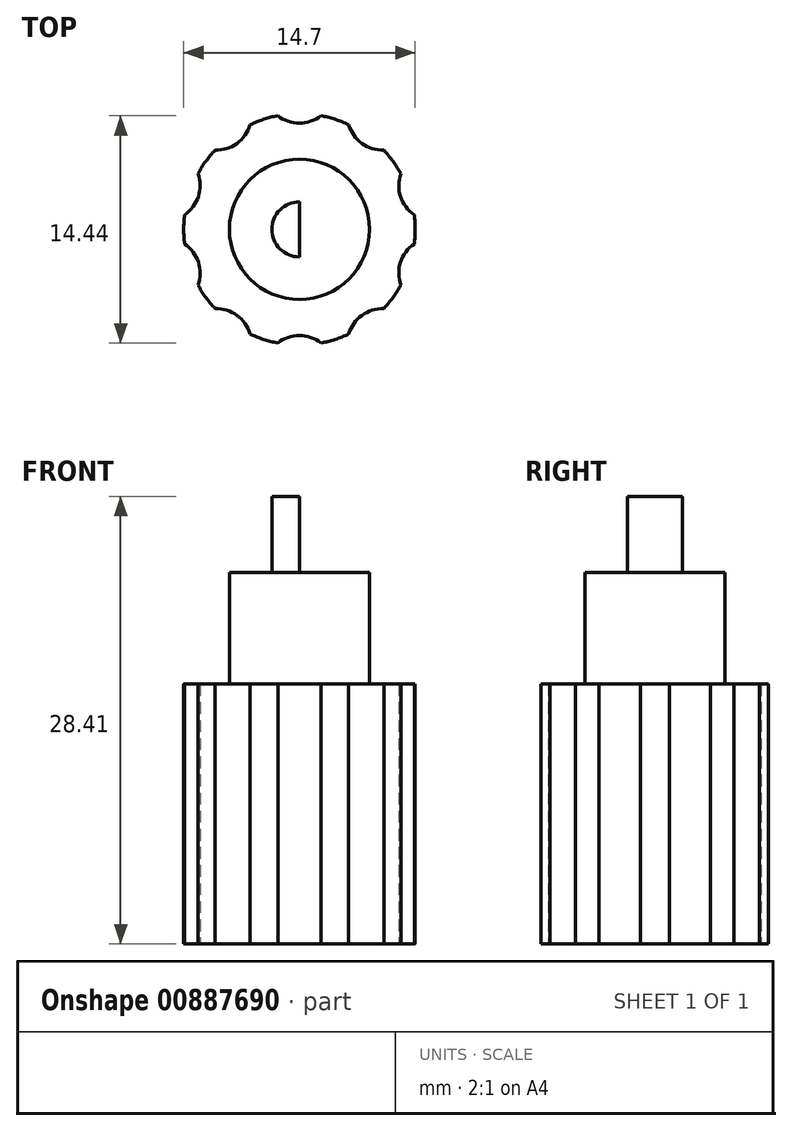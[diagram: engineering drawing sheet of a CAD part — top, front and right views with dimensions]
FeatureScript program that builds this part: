
annotation { "Feature Type Name" : "Feature", "Feature Type Description" : "" }
export const myFeature = defineFeature(function(context is Context, id is Id, definition is map)
    precondition{}
    {
        {
            var Q0;
            Q0=qCreatedBy(makeId("Top.planeOp"),FACE);
            var sketch = newSketch(context, id + "F0", { "sketchPlane" : qUnion([Q0])});
            skCircle(sketch, "E0", {"center": v(0, 0) * mm, "radius": 7.35 * mm});
            skSolve(sketch);
        }
        {
            var Q0;
            Q0 = qSketchRegion(id + "F0", true);
            extrude(context, id + "F1", {"entities" : qUnion([Q0]), "depth" : 16.5 * mm, "offsetDistance" : 25 * mm});
        }
        {
            var Q0;
            Q0=makeQuery(id+"F1.opExtrude","CAP_FACE",FACE,{"disambiguationData":[OSD([sQuery(id+"F0.wireOp",EDGE,"E0")])],"isStart":false});
            var sketch = newSketch(context, id + "F2", { "sketchPlane" : qUnion([Q0])});
            skCircle(sketch, "E1", {"center": v(0, 0) * mm, "radius": 4.45 * mm});
            skSolve(sketch);
        }
        {
            var Q0;
            Q0 = qSketchRegion(id + "F2", true);
            extrude(context, id + "F3", {"entities" : qUnion([Q0]), "operationType" : NewBodyOperationType.ADD, "depth" : 7.08 * mm, "offsetDistance" : 25 * mm});
        }
        {
            var Q0;
            Q0=makeQuery(id+"F3.opExtrude","CAP_FACE",FACE,{"disambiguationData":[OSD([sQuery(id+"F2.wireOp",EDGE,"E1")])],"isStart":false});
            var sketch = newSketch(context, id + "F4", { "sketchPlane" : qUnion([Q0])});
            skSolve(sketch);
        }
        {
            var Q0;
            Q0=makeQuery(id+"F4.imprint","IMPRINT",FACE,{"disambiguationData":[TD([[makeQuery(id+"F4.imprint","IMPRINT",EDGE,{"derivedFrom":makeQuery(id+"F3.opExtrude","CAP_EDGE",EDGE,{"disambiguationData":[OSD([sQuery(id+"F2.wireOp",EDGE,"E1")])],"isStart":false})}),1.0]])]});
            var sketch = newSketch(context, id + "F5", { "sketchPlane" : qUnion([Q0])});
            skArc(sketch, "E2", {"start": v(0, 1.75) * mm, "mid": v(-1.75, 0) * mm, "end": v(0, -1.75) * mm});
            skLineSegment(sketch, "E3", {"start": v(0, -1.75) * mm, "end": v(0, 1.75) * mm});
            skSolve(sketch);
        }
        {
            var Q0;
            Q0 = qSketchRegion(id + "F5", true);
            extrude(context, id + "F6", {"entities" : qUnion([Q0]), "operationType" : NewBodyOperationType.ADD, "depth" : 4.83 * mm, "offsetDistance" : 25 * mm});
        }
        {
            var Q0;
            Q0=makeQuery(id+"F1.opExtrude","CAP_FACE",FACE,{"disambiguationData":[OSD([sQuery(id+"F0.wireOp",EDGE,"E0")])],"isStart":true});
            var sketch = newSketch(context, id + "F7", { "sketchPlane" : qUnion([Q0])});
            skLineSegment(sketch, "E4", {"start": v(0, 0) * mm, "end": v(0, -9) * mm, "construction": true});
            skCircle(sketch, "E5", {"center": v(0, -9) * mm, "radius": 2.25 * mm});
            skCircle(sketch, "E6.1.0", {"center": v(5.3, -7.28) * mm, "radius": 2.25 * mm});
            skCircle(sketch, "E6.2.0", {"center": v(8.56, -2.78) * mm, "radius": 2.25 * mm});
            skCircle(sketch, "E6.3.0", {"center": v(8.56, 2.78) * mm, "radius": 2.25 * mm});
            skCircle(sketch, "E6.4.0", {"center": v(5.3, 7.28) * mm, "radius": 2.25 * mm});
            skCircle(sketch, "E6.5.0", {"center": v(0, 9) * mm, "radius": 2.25 * mm});
            skCircle(sketch, "E6.6.0", {"center": v(-5.3, 7.28) * mm, "radius": 2.25 * mm});
            skCircle(sketch, "E6.7.0", {"center": v(-8.56, 2.78) * mm, "radius": 2.25 * mm});
            skCircle(sketch, "E6.8.0", {"center": v(-8.56, -2.78) * mm, "radius": 2.25 * mm});
            skCircle(sketch, "E6.9.0", {"center": v(-5.3, -7.28) * mm, "radius": 2.25 * mm});
            skPoint(sketch, "E6.center", {"position": v(0, 0) * mm});
            skSolve(sketch);
        }
        {
            var Q0;
            Q0 = qSketchRegion(id + "F7", true);
            extrude(context, id + "F8", {"entities" : qUnion([Q0]), "operationType" : NewBodyOperationType.REMOVE, "oppositeDirection" : true, "depth" : 25 * mm, "offsetDistance" : 25 * mm});
        }
        {
            var Q0;
            {var subQ0=sQuery(id+"F7.wireOp",EDGE,"E6.2.0");var subQ1=makeQuery(id+"F1.opExtrude","CAP_EDGE",EDGE,{"disambiguationData":[OSD([sQuery(id+"F0.wireOp",EDGE,"E0")])],"isStart":true});var subQ2=makeQuery(id+"F7.imprint","INTERSECT",VERTEX,{"disambiguationData":[OD(0.0)],"derivedFrom":[subQ1,subQ0]});Q0=makeQuery(id+"F7.imprint","IMPRINT",FACE,{"disambiguationData":[TD([[makeQuery(id+"F7.imprint","IMPRINT",EDGE,{"disambiguationData":[TD([[subQ2,1.0]])],"derivedFrom":subQ0}),1.0]])]});}
            var Q1;
            {var subQ0=sQuery(id+"F7.wireOp",EDGE,"E6.1.0");var subQ1=makeQuery(id+"F1.opExtrude","CAP_EDGE",EDGE,{"disambiguationData":[OSD([sQuery(id+"F0.wireOp",EDGE,"E0")])],"isStart":true});var subQ2=makeQuery(id+"F7.imprint","INTERSECT",VERTEX,{"disambiguationData":[OD(0.0)],"derivedFrom":[subQ1,subQ0]});Q1=makeQuery(id+"F7.imprint","IMPRINT",FACE,{"disambiguationData":[TD([[makeQuery(id+"F7.imprint","IMPRINT",EDGE,{"disambiguationData":[TD([[subQ2,-1.0]])],"derivedFrom":subQ0}),1.0]])]});}
            var Q2;
            {var subQ0=sQuery(id+"F7.wireOp",EDGE,"E5");var subQ1=makeQuery(id+"F1.opExtrude","CAP_EDGE",EDGE,{"disambiguationData":[OSD([sQuery(id+"F0.wireOp",EDGE,"E0")])],"isStart":true});var subQ2=makeQuery(id+"F7.imprint","INTERSECT",VERTEX,{"disambiguationData":[OD(0.0)],"derivedFrom":[subQ1,subQ0]});Q2=makeQuery(id+"F7.imprint","IMPRINT",FACE,{"disambiguationData":[TD([[makeQuery(id+"F7.imprint","IMPRINT",EDGE,{"disambiguationData":[TD([[subQ2,-1.0]])],"derivedFrom":subQ0}),1.0]])]});}
            var Q3;
            {var subQ0=sQuery(id+"F7.wireOp",EDGE,"E6.9.0");var subQ1=makeQuery(id+"F1.opExtrude","CAP_EDGE",EDGE,{"disambiguationData":[OSD([sQuery(id+"F0.wireOp",EDGE,"E0")])],"isStart":true});var subQ2=makeQuery(id+"F7.imprint","INTERSECT",VERTEX,{"disambiguationData":[OD(0.0)],"derivedFrom":[subQ1,subQ0]});Q3=makeQuery(id+"F7.imprint","IMPRINT",FACE,{"disambiguationData":[TD([[makeQuery(id+"F7.imprint","IMPRINT",EDGE,{"disambiguationData":[TD([[subQ2,-1.0]])],"derivedFrom":subQ0}),1.0]])]});}
            var Q4;
            {var subQ0=sQuery(id+"F7.wireOp",EDGE,"E6.8.0");var subQ1=makeQuery(id+"F1.opExtrude","CAP_EDGE",EDGE,{"disambiguationData":[OSD([sQuery(id+"F0.wireOp",EDGE,"E0")])],"isStart":true});var subQ2=makeQuery(id+"F7.imprint","INTERSECT",VERTEX,{"disambiguationData":[OD(0.0)],"derivedFrom":[subQ1,subQ0]});Q4=makeQuery(id+"F7.imprint","IMPRINT",FACE,{"disambiguationData":[TD([[makeQuery(id+"F7.imprint","IMPRINT",EDGE,{"disambiguationData":[TD([[subQ2,-1.0]])],"derivedFrom":subQ0}),1.0]])]});}
            var Q5;
            {var subQ0=sQuery(id+"F7.wireOp",EDGE,"E6.7.0");var subQ1=makeQuery(id+"F1.opExtrude","CAP_EDGE",EDGE,{"disambiguationData":[OSD([sQuery(id+"F0.wireOp",EDGE,"E0")])],"isStart":true});var subQ2=makeQuery(id+"F7.imprint","INTERSECT",VERTEX,{"disambiguationData":[OD(0.0)],"derivedFrom":[subQ1,subQ0]});Q5=makeQuery(id+"F7.imprint","IMPRINT",FACE,{"disambiguationData":[TD([[makeQuery(id+"F7.imprint","IMPRINT",EDGE,{"disambiguationData":[TD([[subQ2,-1.0]])],"derivedFrom":subQ0}),1.0]])]});}
            var Q6;
            {var subQ0=sQuery(id+"F7.wireOp",EDGE,"E6.6.0");var subQ1=makeQuery(id+"F1.opExtrude","CAP_EDGE",EDGE,{"disambiguationData":[OSD([sQuery(id+"F0.wireOp",EDGE,"E0")])],"isStart":true});var subQ2=makeQuery(id+"F7.imprint","INTERSECT",VERTEX,{"disambiguationData":[OD(0.0)],"derivedFrom":[subQ1,subQ0]});Q6=makeQuery(id+"F7.imprint","IMPRINT",FACE,{"disambiguationData":[TD([[makeQuery(id+"F7.imprint","IMPRINT",EDGE,{"disambiguationData":[TD([[subQ2,1.0]])],"derivedFrom":subQ0}),1.0]])]});}
            var Q7;
            {var subQ0=sQuery(id+"F7.wireOp",EDGE,"E6.5.0");var subQ1=makeQuery(id+"F1.opExtrude","CAP_EDGE",EDGE,{"disambiguationData":[OSD([sQuery(id+"F0.wireOp",EDGE,"E0")])],"isStart":true});var subQ2=makeQuery(id+"F7.imprint","INTERSECT",VERTEX,{"disambiguationData":[OD(0.0)],"derivedFrom":[subQ1,subQ0]});Q7=makeQuery(id+"F7.imprint","IMPRINT",FACE,{"disambiguationData":[TD([[makeQuery(id+"F7.imprint","IMPRINT",EDGE,{"disambiguationData":[TD([[subQ2,1.0]])],"derivedFrom":subQ0}),1.0]])]});}
            var Q8;
            {var subQ0=sQuery(id+"F7.wireOp",EDGE,"E6.4.0");var subQ1=makeQuery(id+"F1.opExtrude","CAP_EDGE",EDGE,{"disambiguationData":[OSD([sQuery(id+"F0.wireOp",EDGE,"E0")])],"isStart":true});var subQ2=makeQuery(id+"F7.imprint","INTERSECT",VERTEX,{"disambiguationData":[OD(0.0)],"derivedFrom":[subQ1,subQ0]});Q8=makeQuery(id+"F7.imprint","IMPRINT",FACE,{"disambiguationData":[TD([[makeQuery(id+"F7.imprint","IMPRINT",EDGE,{"disambiguationData":[TD([[subQ2,1.0]])],"derivedFrom":subQ0}),1.0]])]});}
            var Q9;
            {var subQ0=sQuery(id+"F7.wireOp",EDGE,"E6.3.0");var subQ1=makeQuery(id+"F1.opExtrude","CAP_EDGE",EDGE,{"disambiguationData":[OSD([sQuery(id+"F0.wireOp",EDGE,"E0")])],"isStart":true});var subQ2=makeQuery(id+"F7.imprint","INTERSECT",VERTEX,{"disambiguationData":[OD(0.0)],"derivedFrom":[subQ1,subQ0]});Q9=makeQuery(id+"F7.imprint","IMPRINT",FACE,{"disambiguationData":[TD([[makeQuery(id+"F7.imprint","IMPRINT",EDGE,{"disambiguationData":[TD([[subQ2,1.0]])],"derivedFrom":subQ0}),1.0]])]});}
            extrude(context, id + "F9", {"entities" : qUnion([Q0, Q1, Q2, Q3, Q4, Q5, Q6, Q7, Q8, Q9]), "operationType" : NewBodyOperationType.REMOVE, "oppositeDirection" : true, "depth" : 25 * mm, "offsetDistance" : 25 * mm});
        }
    });
